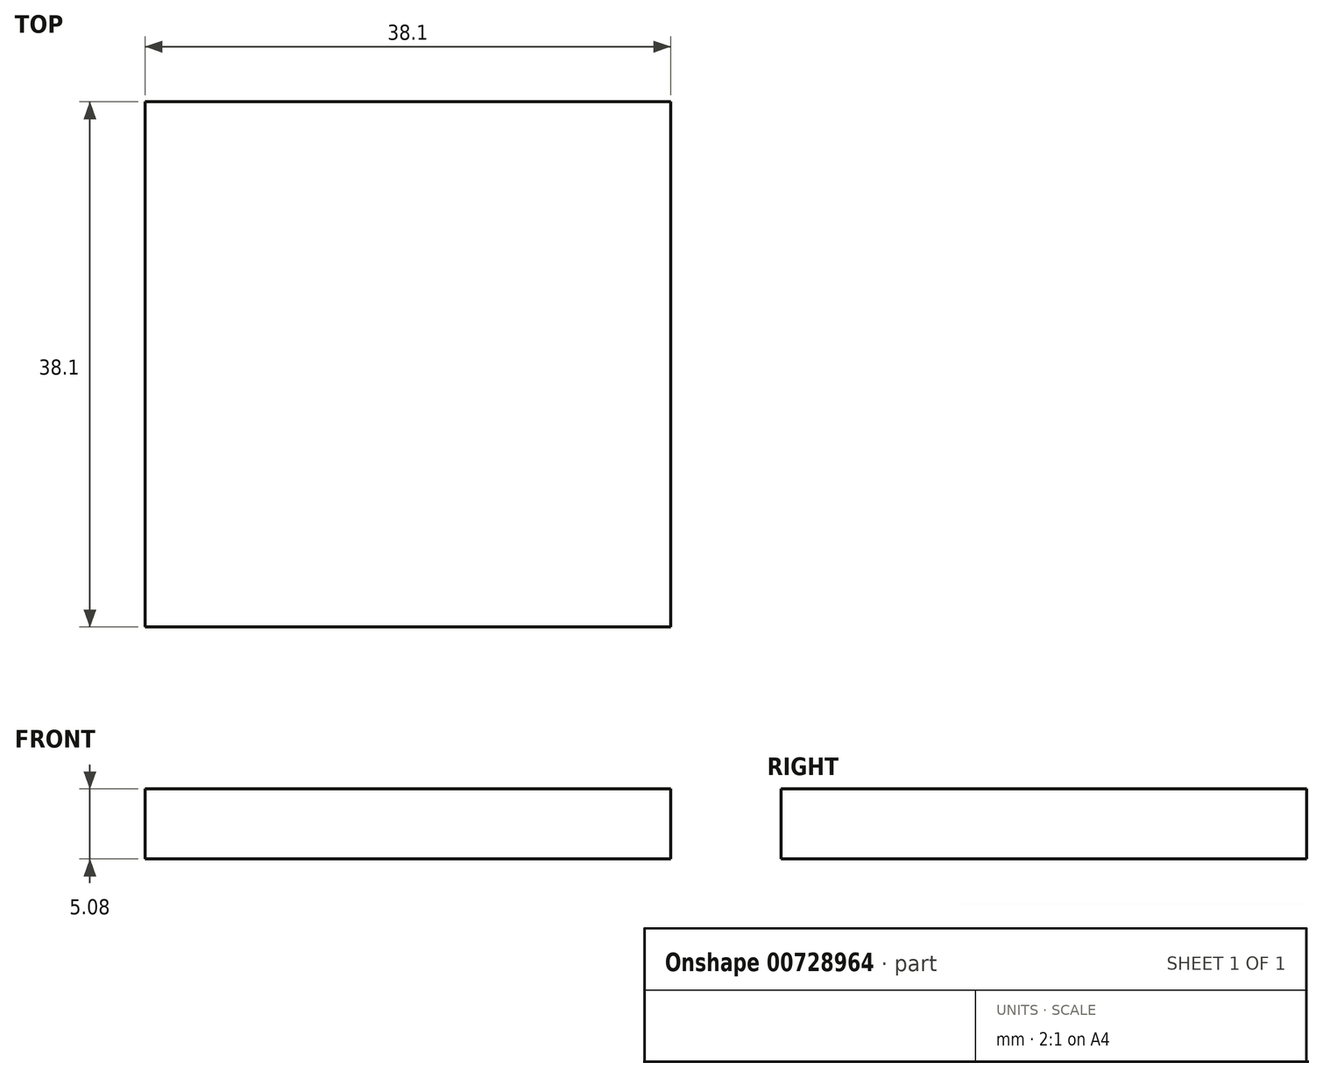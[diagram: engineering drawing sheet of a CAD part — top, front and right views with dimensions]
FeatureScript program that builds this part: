
annotation { "Feature Type Name" : "Feature", "Feature Type Description" : "" }
export const myFeature = defineFeature(function(context is Context, id is Id, definition is map)
    precondition{}
    {
        {
            var Q0;
            Q0=qCreatedBy(makeId("Top.planeOp"),FACE);
            var sketch = newSketch(context, id + "F0", { "sketchPlane" : qUnion([Q0])});
            skLineSegment(sketch, "E0.bottom", {"start": v(19.05, 19.05) * mm, "end": v(-19.05, 19.05) * mm});
            skLineSegment(sketch, "E0.top", {"start": v(19.05, -19.05) * mm, "end": v(-19.05, -19.05) * mm});
            skLineSegment(sketch, "E0.left", {"start": v(19.05, 19.05) * mm, "end": v(19.05, -19.05) * mm});
            skLineSegment(sketch, "E0.right", {"start": v(-19.05, 19.05) * mm, "end": v(-19.05, -19.05) * mm});
            skPoint(sketch, "E0.middle", {"position": v(0, 0) * mm});
            skSolve(sketch);
        }
        {
            var Q0;
            Q0=makeQuery(id+"F0.imprint","IMPRINT",FACE,{"disambiguationData":[TD([[makeQuery(id+"F0.imprint","IMPRINT",EDGE,{"derivedFrom":sQuery(id+"F0.wireOp",EDGE,"E0.bottom")}),1.0]])]});
            extrude(context, id + "F1", {"entities" : qUnion([Q0]), "depth" : 5.08 * mm, "offsetDistance" : 25.4 * mm});
        }
    });
